AUTODESK INVENTOR PART (.ipt)
format: ipt  version: 2017 (Build 210142000, 142)  size: 119,808 bytes
history: native  units: mm
features: reference x16, other x4, extrude x1, sketch x1
ambient origin geometry x8: Origin, YZ Plane, XZ Plane, XY Plane, X Axis, Y Axis, Z Axis, Center Point
bodies: Body1 (feature_tree)
feature tree (22):
  other  "Sólido1"
  extrude  "Extrusión1"  TaperAngle=45.0deg  [1 undecoded]
  sketch  "Boceto1"  dims[d0=13.05mm d1=45.0deg d2=6.0mm d3=8.0mm d4=6.0mm d5=7.0mm d6=120.0deg d7=5.0mm d8=4.0mm d9=0.0mm]
  reference  "Referencia1"
  reference  "Referencia3"
  reference  "Referencia6"
  reference  "Referencia8"
  reference  "Referencia9"
  reference  "Referencia10"
  reference  "Referencia11"
  reference  "Referencia12"
  reference  "Referencia13"
  reference  "Referencia14"
  reference  "Referencia15"
  reference  "Referencia16"
  reference  "Referencia17"
  reference  "Referencia18"
  reference  "Referencia19"
  reference  "Referencia20"
  other  "<userpath>\Documents\GitHub\actor-re-actor\models\inventor-caja\Case\Case-D.iam"
  other  "Case-D.iam"
  other  "Carcasa:1"
note: 1 required parameter value undecoded (feature->parameter linkage not recoverable at this tier; creation-order binding heuristic only, values carry confidence <= 0.55)
